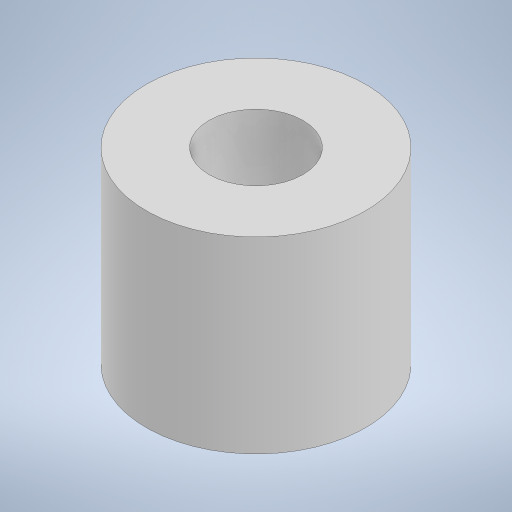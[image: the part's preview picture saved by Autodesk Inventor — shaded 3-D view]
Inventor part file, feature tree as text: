
AUTODESK INVENTOR PART (.ipt)
format: ipt  version: 2024 (Build 280153000, 153)  size: 502,784 bytes
history: native  units: mm
features: extrude x2, sketch x2
ambient origin geometry x8: Origin, YZ Plane, XZ Plane, XY Plane, X Axis, Y Axis, Z Axis, Center Point
bodies: Solid1 (feature_tree)
feature tree (4):
  extrude  "Extrusion1"  Depth=6.0mm TaperAngle=0.0deg
  extrude  "Extrusion2"  Depth=6.0mm TaperAngle=0.0deg
  sketch  "Sketch1"  dims[d0=7.0mm d1=6.0mm d2=0.0mm]
  sketch  "Sketch2"  dims[d3=3.0mm d4=6.0mm d5=0.0mm]
